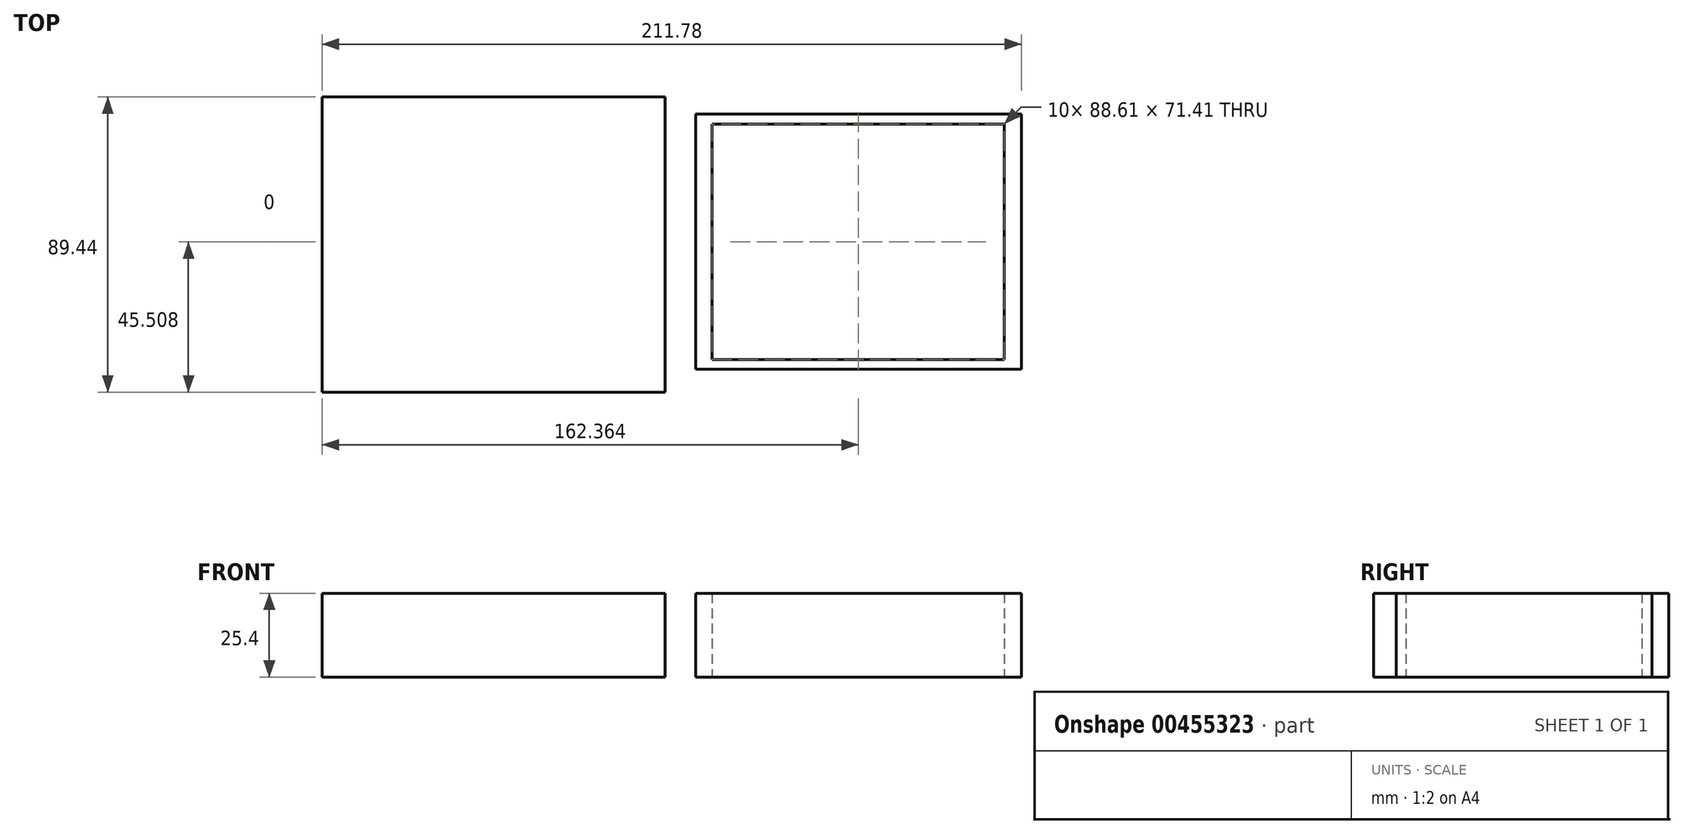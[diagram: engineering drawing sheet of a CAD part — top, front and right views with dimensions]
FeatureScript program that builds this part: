
annotation { "Feature Type Name" : "Feature", "Feature Type Description" : "" }
export const myFeature = defineFeature(function(context is Context, id is Id, definition is map)
    precondition{}
    {
        {
            var Q0;
            Q0=qCreatedBy(makeId("Top.planeOp"),FACE);
            var sketch = newSketch(context, id + "F0", { "sketchPlane" : qUnion([Q0])});
            skLineSegment(sketch, "E0.bottom", {"start": v(-43.43, 35.41) * mm, "end": v(45.18, 35.41) * mm});
            skLineSegment(sketch, "E0.top", {"start": v(-43.43, -36) * mm, "end": v(45.18, -36) * mm});
            skLineSegment(sketch, "E0.left", {"start": v(-43.43, 35.41) * mm, "end": v(-43.43, -36) * mm});
            skLineSegment(sketch, "E0.right", {"start": v(45.18, 35.41) * mm, "end": v(45.18, -36) * mm});
            skLineSegment(sketch, "E1.bottom", {"start": v(-48.39, 38.52) * mm, "end": v(50.29, 38.52) * mm});
            skLineSegment(sketch, "E1.top", {"start": v(-48.39, -38.93) * mm, "end": v(50.29, -38.93) * mm});
            skLineSegment(sketch, "E1.left", {"start": v(-48.39, 38.52) * mm, "end": v(-48.39, -38.93) * mm});
            skLineSegment(sketch, "E1.right", {"start": v(50.29, 38.52) * mm, "end": v(50.29, -38.93) * mm});
            skSolve(sketch);
        }
        {
            var Q0;
            Q0 = qSketchRegion(id + "F0", true);
            extrude(context, id + "F1", {"entities" : qUnion([Q0]), "depth" : 25.4 * mm});
        }
        {
            var Q0;
            Q0=qCreatedBy(makeId("Top.planeOp"),FACE);
            var sketch = newSketch(context, id + "F2", { "sketchPlane" : qUnion([Q0])});
            skLineSegment(sketch, "E2.bottom", {"start": v(-161.5, 43.64) * mm, "end": v(-57.6, 43.64) * mm});
            skLineSegment(sketch, "E2.top", {"start": v(-161.5, -45.8) * mm, "end": v(-57.6, -45.8) * mm});
            skLineSegment(sketch, "E2.left", {"start": v(-161.5, 43.64) * mm, "end": v(-161.5, -45.8) * mm});
            skLineSegment(sketch, "E2.right", {"start": v(-57.6, 43.64) * mm, "end": v(-57.6, -45.8) * mm});
            skSolve(sketch);
        }
        {
            var Q0;
            Q0=makeQuery(id+"F2.imprint","IMPRINT",FACE,{"disambiguationData":[TD([[makeQuery(id+"F2.imprint","IMPRINT",EDGE,{"derivedFrom":sQuery(id+"F2.wireOp",EDGE,"E2.bottom")}),-1.0]])]});
            extrude(context, id + "F3", {"entities" : qUnion([Q0]), "depth" : 25.4 * mm});
        }
    });
